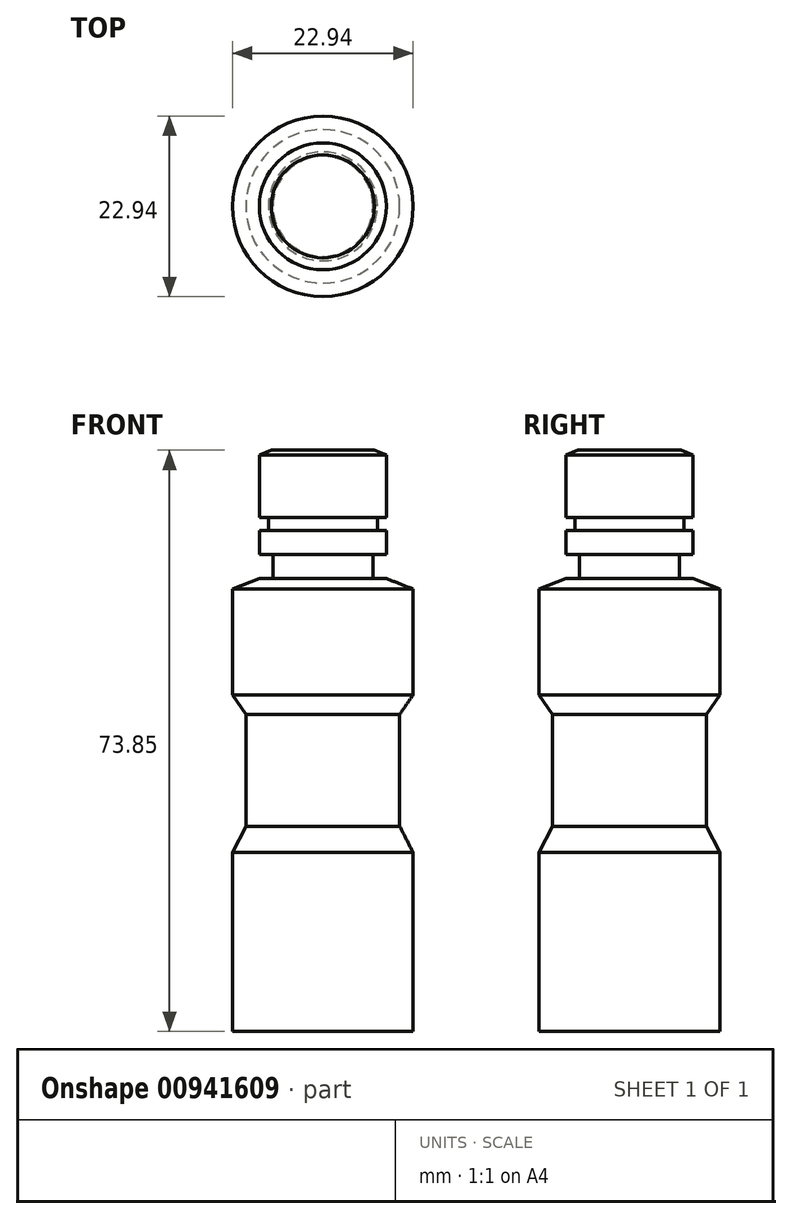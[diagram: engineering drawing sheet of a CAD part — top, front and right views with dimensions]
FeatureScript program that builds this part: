
annotation { "Feature Type Name" : "Feature", "Feature Type Description" : "" }
export const myFeature = defineFeature(function(context is Context, id is Id, definition is map)
    precondition{}
    {
        {
            var Q0;
            Q0=qCreatedBy(makeId("Front.planeOp"),FACE);
            var sketch = newSketch(context, id + "F0", { "sketchPlane" : qUnion([Q0])});
            skLineSegment(sketch, "E0", {"start": v(0, 0) * mm, "end": v(-11.47, 0) * mm});
            skLineSegment(sketch, "E1", {"start": v(-11.47, 0) * mm, "end": v(-11.47, 22.72) * mm});
            skLineSegment(sketch, "E2", {"start": v(-11.47, 22.72) * mm, "end": v(-9.76, 26.07) * mm});
            skLineSegment(sketch, "E3", {"start": v(-9.76, 26.07) * mm, "end": v(-9.76, 40.29) * mm});
            skLineSegment(sketch, "E4", {"start": v(-9.76, 40.29) * mm, "end": v(-11.47, 42.75) * mm});
            skLineSegment(sketch, "E5", {"start": v(-11.47, 42.75) * mm, "end": v(-11.47, 56.2) * mm});
            skLineSegment(sketch, "E6", {"start": v(-11.47, 56.2) * mm, "end": v(-8.06, 57.54) * mm});
            skLineSegment(sketch, "E7", {"start": v(-8.06, 57.54) * mm, "end": v(-6.35, 57.54) * mm});
            skLineSegment(sketch, "E8", {"start": v(-6.35, 57.54) * mm, "end": v(-6.35, 60.58) * mm});
            skLineSegment(sketch, "E9", {"start": v(-6.35, 60.58) * mm, "end": v(-8.06, 60.58) * mm});
            skLineSegment(sketch, "E10", {"start": v(-8.06, 60.58) * mm, "end": v(-8.06, 63.6) * mm});
            skLineSegment(sketch, "E11", {"start": v(-8.06, 63.6) * mm, "end": v(-6.92, 63.6) * mm});
            skLineSegment(sketch, "E12", {"start": v(-6.92, 63.6) * mm, "end": v(-6.92, 65.32) * mm});
            skLineSegment(sketch, "E13", {"start": v(-6.92, 65.32) * mm, "end": v(-8.06, 65.32) * mm});
            skLineSegment(sketch, "E14", {"start": v(-8.06, 65.32) * mm, "end": v(-8.06, 73.25) * mm});
            skLineSegment(sketch, "E15", {"start": v(-6.54, 73.85) * mm, "end": v(-8.06, 73.25) * mm});
            skLineSegment(sketch, "E16", {"start": v(-6.54, 73.85) * mm, "end": v(0, 73.85) * mm});
            skLineSegment(sketch, "E17", {"start": v(0, 73.85) * mm, "end": v(0, 0) * mm});
            skSolve(sketch);
        }
        {
            var Q0;
            Q0=makeQuery(id+"F0.imprint","IMPRINT",FACE,{"disambiguationData":[TD([[makeQuery(id+"F0.imprint","IMPRINT",EDGE,{"derivedFrom":sQuery(id+"F0.wireOp",EDGE,"E0")}),-1.0]])]});
            var Q1;
            Q1=sQuery(id+"F0.wireOp",EDGE,"E17");
            revolve(context, id + "F1", {"surfaceOperationType" : NewSurfaceOperationType.NEW, "entities" : qUnion([Q0]), "axis" : qUnion([Q1]), "revolveType" : RevolveType.FULL});
        }
    });
